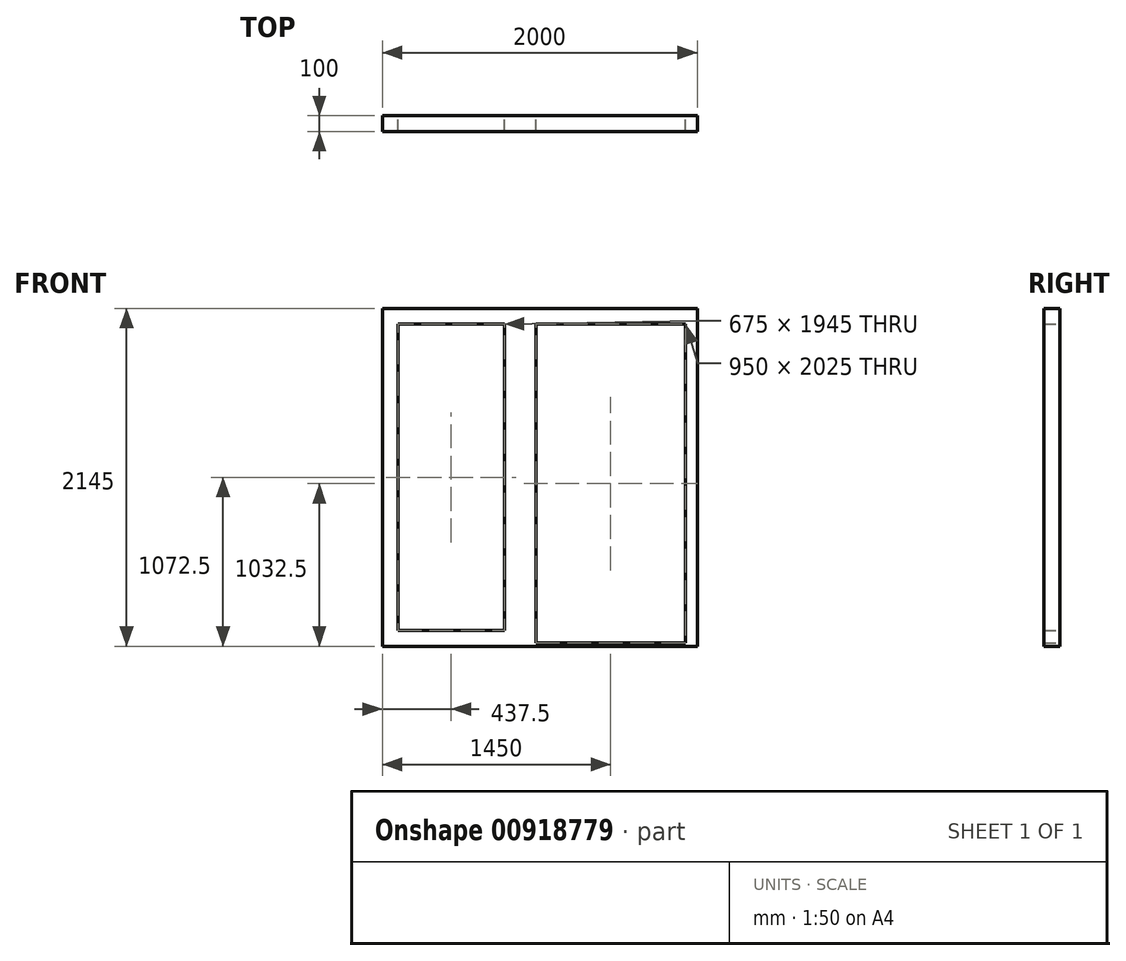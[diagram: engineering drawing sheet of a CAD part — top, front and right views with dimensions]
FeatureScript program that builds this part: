
annotation { "Feature Type Name" : "Feature", "Feature Type Description" : "" }
export const myFeature = defineFeature(function(context is Context, id is Id, definition is map)
    precondition{}
    {
        {
            var Q0;
            Q0=qCreatedBy(makeId("Front.planeOp"),FACE);
            var sketch = newSketch(context, id + "F0", { "sketchPlane" : qUnion([Q0])});
            skLineSegment(sketch, "E0.bottom", {"start": v(0, 0) * mm, "end": v(2000, 0) * mm});
            skLineSegment(sketch, "E0.top", {"start": v(0, 2145) * mm, "end": v(2000, 2145) * mm});
            skLineSegment(sketch, "E0.left", {"start": v(0, 0) * mm, "end": v(0, 2145) * mm});
            skLineSegment(sketch, "E0.right", {"start": v(2000, 0) * mm, "end": v(2000, 2145) * mm});
            skLineSegment(sketch, "E1.bottom", {"start": v(975, 20) * mm, "end": v(1925, 20) * mm});
            skLineSegment(sketch, "E1.top", {"start": v(975, 2045) * mm, "end": v(1925, 2045) * mm});
            skLineSegment(sketch, "E1.left", {"start": v(975, 20) * mm, "end": v(975, 2045) * mm});
            skLineSegment(sketch, "E1.right", {"start": v(1925, 20) * mm, "end": v(1925, 2045) * mm});
            skLineSegment(sketch, "E2.bottom", {"start": v(775, 2045) * mm, "end": v(100, 2045) * mm});
            skLineSegment(sketch, "E2.top", {"start": v(775, 100) * mm, "end": v(100, 100) * mm});
            skLineSegment(sketch, "E2.left", {"start": v(775, 2045) * mm, "end": v(775, 100) * mm});
            skLineSegment(sketch, "E2.right", {"start": v(100, 2045) * mm, "end": v(100, 100) * mm});
            skSolve(sketch);
        }
        {
            var Q0;
            Q0=makeQuery(id+"F0.imprint","IMPRINT",FACE,{"disambiguationData":[TD([[makeQuery(id+"F0.imprint","IMPRINT",EDGE,{"derivedFrom":sQuery(id+"F0.wireOp",EDGE,"E0.bottom")}),1.0]])]});
            extrude(context, id + "F1", {"entities" : qUnion([Q0]), "depth" : 100 * mm, "offsetDistance" : 25 * mm});
        }
    });
